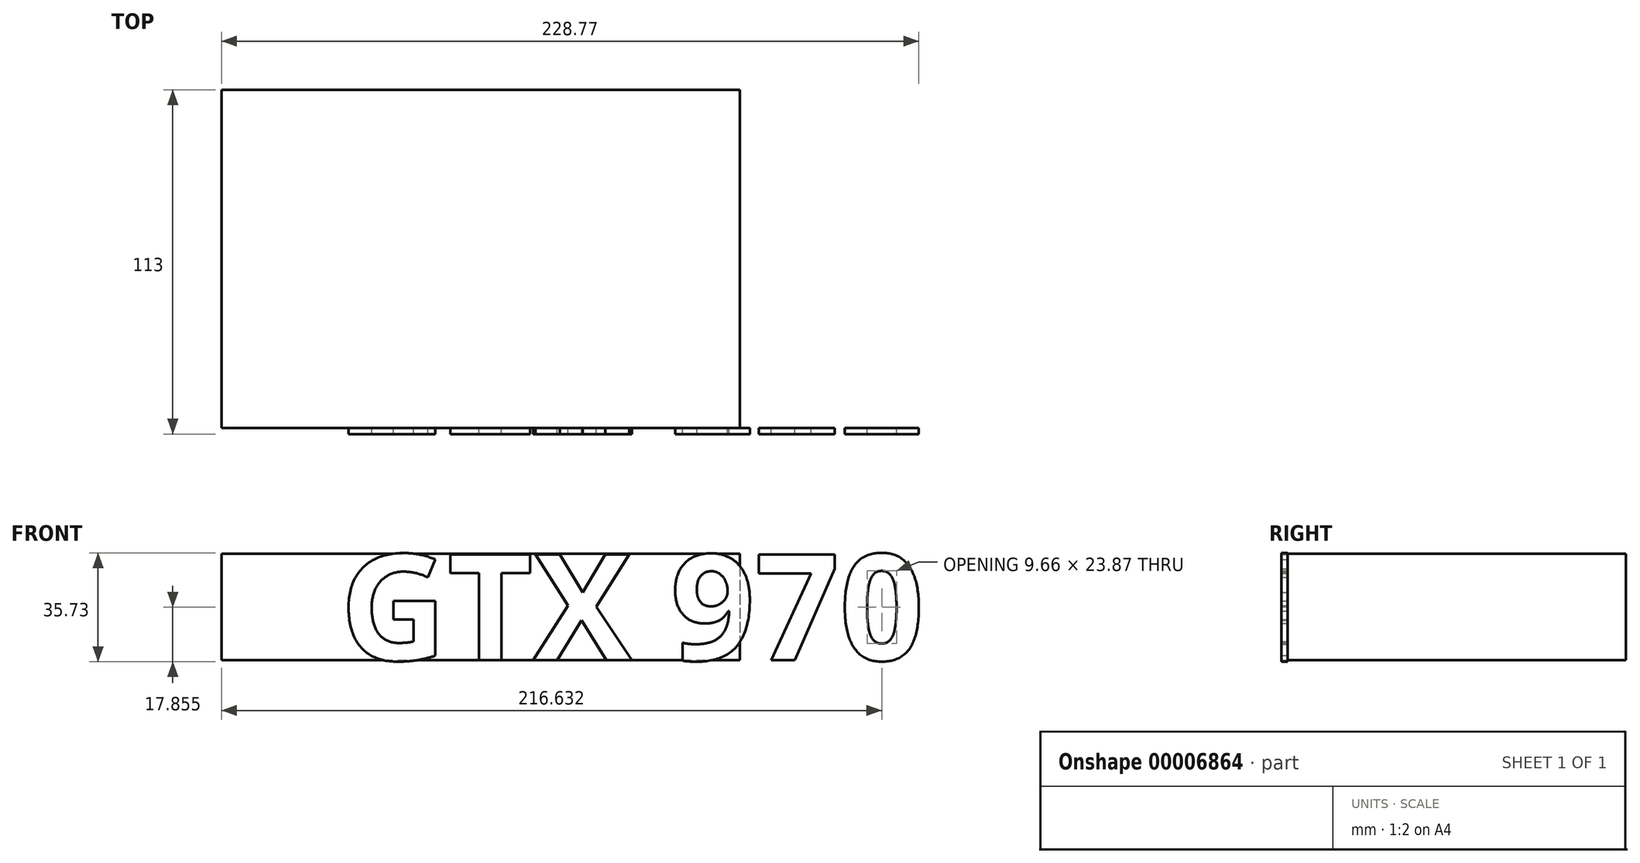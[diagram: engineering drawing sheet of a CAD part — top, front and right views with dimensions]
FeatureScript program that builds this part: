
annotation { "Feature Type Name" : "Feature", "Feature Type Description" : "" }
export const myFeature = defineFeature(function(context is Context, id is Id, definition is map)
    precondition{}
    {
        {
            var Q0;
            Q0=qCreatedBy(makeId("Top.planeOp"),FACE);
            var sketch = newSketch(context, id + "F0", { "sketchPlane" : qUnion([Q0])});
            skLineSegment(sketch, "E0.bottom", {"start": v(-100.66, 0) * mm, "end": v(69.34, 0) * mm});
            skLineSegment(sketch, "E0.top", {"start": v(-100.66, 111) * mm, "end": v(69.34, 111) * mm});
            skLineSegment(sketch, "E0.left", {"start": v(-100.66, 0) * mm, "end": v(-100.66, 111) * mm});
            skLineSegment(sketch, "E0.right", {"start": v(69.34, 0) * mm, "end": v(69.34, 111) * mm});
            skSolve(sketch);
        }
        {
            var Q0;
            Q0 = qSketchRegion(id + "F0", true);
            extrude(context, id + "F1", {"entities" : qUnion([Q0]), "depth" : 35 * mm});
        }
        {
            var Q0;
            Q0=makeQuery(id+"F1.opExtrude","SWEPT_FACE",FACE,{"disambiguationData":[OSD([sQuery(id+"F0.wireOp",EDGE,"E0.bottom")])]});
            var sketch = newSketch(context, id + "F2", { "sketchPlane" : qUnion([Q0])});
            skText(sketch, "E1", { "text": "GTX 970", "fontName": "OpenSans-Bold.ttf"});
            const initialGuessF2  = {"E1": [-0.0618, 0, 1, 0, 0.035]};
            skSetInitialGuess(sketch, initialGuessF2);
            skSolve(sketch);
        }
        {
            var Q0;
            Q0 = qSketchRegion(id + "F2", true);
            extrude(context, id + "F3", {"entities" : qUnion([Q0]), "operationType" : NewBodyOperationType.ADD, "depth" : 2 * mm});
        }
    });
